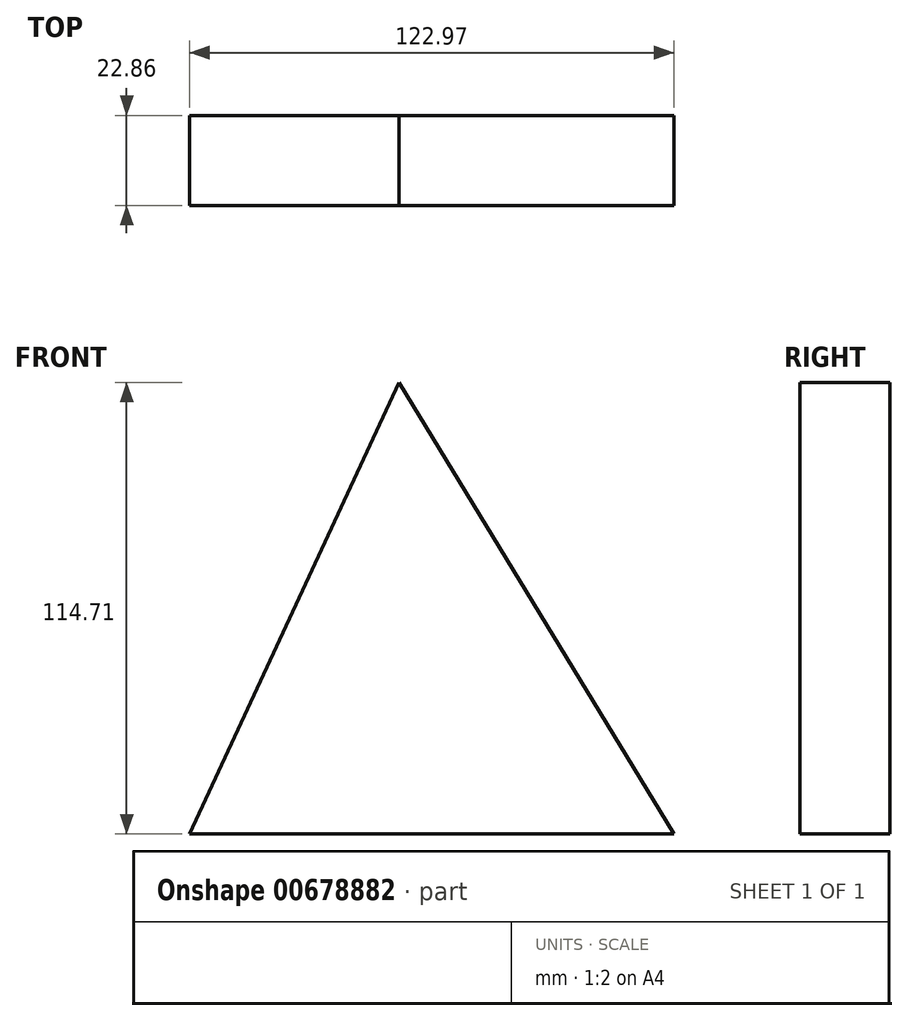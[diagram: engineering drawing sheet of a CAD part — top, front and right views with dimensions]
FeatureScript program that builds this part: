
annotation { "Feature Type Name" : "Feature", "Feature Type Description" : "" }
export const myFeature = defineFeature(function(context is Context, id is Id, definition is map)
    precondition{}
    {
        {
            var Q0;
            Q0=qCreatedBy(makeId("Front.planeOp"),FACE);
            var sketch = newSketch(context, id + "F0", { "sketchPlane" : qUnion([Q0])});
            skLineSegment(sketch, "E0", {"start": v(-53.2, -46.86) * mm, "end": v(0, 67.85) * mm});
            skLineSegment(sketch, "E1", {"start": v(0, 67.85) * mm, "end": v(71.28, -49.36) * mm});
            skLineSegment(sketch, "E2", {"start": v(-53.2, -46.86) * mm, "end": v(69.77, -46.86) * mm});
            skSolve(sketch);
        }
        {
            var Q0;
            Q0 = qSketchRegion(id + "F0", true);
            extrude(context, id + "F1", {"entities" : qUnion([Q0]), "oppositeDirection" : true, "depth" : 22.86 * mm, "offsetDistance" : 25.4 * mm});
        }
    });
